# Revit family: EU_SINGLE_ODU_UB1_Ver.1.1
name_source: partatom
category: Mechanical Equipment
revit_build: Autodesk Revit 2016 (Build: 20150220_1215(x64)
units: mm (PartAtom-declared; Revit-internal decimal feet)

## family parameters
Always vertical = Yes
Cut with Voids When Loaded = No
Part Type = Normal
Room Calculation Point = No
Round Connector Dimension = Use Radius
Shared = No
Work Plane-Based = No

## types (26) — shared parameters
Fan Grill Height = 653.88 mm
Fan Grill Length = 580.00 mm
Free Content Downloads = -
Location = -
Manufacturer = SAMSUNG
Manufacturer Metadata = -
Notes = -
Product Documentation Link = -
Product Page URL = -
Sales Rep Locator = -
Serial Number = -
Subscribe for Update Alerts = -
System Served = -
URL = www.samsung.com

## per-type parameters (varying)
| type | Model | Net Weight | Refrigerant Type |
| 9.00 kW, 380-415V, HEAT PUMP | AC090MXADNH/EU | 72.00 kg | R410A |
| 10.00 kW, 380-415V, HEAT PUMP | AC100MXADNH/EU | 72.00 kg | R410A |
| 12.00 kW, 380-415V, HEAT PUMP | AC120MXADNH/EU | 77.00 kg | R410A |
| 10.00 kW, 220-240V, HEAT PUMP - A | AC100KXADEH/EU | 72.00 kg | R410A |
| 9.00 kW, 220-240V, HEAT PUMP | AC090MXADKH/EU | 72.00 kg | R410A |
| 10.00 kW, 220-240V, HEAT PUMP - B | AC100MXADKH/EU | 72.00 kg | R410A |
| 12.00 kW, 220-240V, HEAT PUMP(구모델) | AC120MXADKH/EU | 77.00 kg | R410A |
| 12.00 kW, 220-240V, HEAT PUMP(신모델) | AC120MXADKH/EU | 77.00 kg | R410A |
| Single Heat Pump, 10.0kW, 220-240, R32, AC100RN4DKG/EU | AC100RXADKG/EU | 72.00 kg | R32 |
| Single Heat Pump, 10.0kW, 380-415, R32, AC100RN4DKG/EU | AC100RXADNG/EU | 72.00 kg | R33 |
| Single Heat Pump, 12.0kW, 220-240, R32, AC120RN4DKG/EU | AC120RXADKG/EU | 77.00 kg | R34 |
| Single Heat Pump, 12.0kW, 380-415, R32, AC120RN4DKG/EU | AC120RXADNG/EU | 77.00 kg | R35 |
| Single Heat Pump, 10.0kW, 220-240, R32, AC100RN4PKG/EU | AC100RXADKG/EU | 72.00 kg | R38 |
| Single Heat Pump, 10.0kW, 380-415, R32, AC100RN4PKG/EU | AC100RXADNG/EU | 72.00 kg | R39 |
| Single Heat Pump, 12.0kW, 220-240, R32, AC120RN4PKG/EU | AC120RXADKG/EU | 77.00 kg | R40 |
| Single Heat Pump, 12.0kW, 380-415, R32, AC120RN4PKG/EU | AC120RXADNG/EU | 77.00 kg | R41 |
| Single Heat Pump, 10.0kW, 220-240, R32, AC100RNMDKG/EU | AC100RXADKG/EU | 72.00 kg | R44 |
| Single Heat Pump, 10.0kW, 380-415, R32, AC100RNMDKG/EU | AC100RXADNG/EU | 72.00 kg | R45 |
| Single Heat Pump, 12.0kW, 220-240, R32, AC120RNMDKG/EU | AC120RXADKG/EU | 77.00 kg | R46 |
| Single Heat Pump, 12.0kW, 380-415, R32, AC120RNMDKG/EU | AC120RXADNG/EU | 77.00 kg | R47 |
| Single Heat Pump, 10.0kW, 220-240, R32, AC100RNCDKG/EU | AC100RXADKG/EU | 72.00 kg | R50 |
| Single Heat Pump, 10.0kW, 380-415, R32, AC100RNCDKG/EU | AC100RXADNG/EU | 72.00 kg | R51 |
| Single Heat Pump, 12.0kW, 220-240, R32, AC120RNCDKG/EU | AC120RXADKG/EU | 77.00 kg | R52 |
| Single Heat Pump, 12.0kW, 380-415, R32, AC120RNCDKG/EU | AC120RXADNG/EU | 77.00 kg | R53 |
| Single Heat Pump, 10.0kW, 220-240, R32, AC100RNTDKG/EU | AC100RXADKG/EU | 72.00 kg | R56 |
| Single Heat Pump, 10.0kW, 380-415, R32, AC100RNTDKG/EU | AC100RXADNG/EU | 72.00 kg | R57 |

## geometry (parser evidence)
native form markers: Sweep x13
no freeform markers — native parametric forms only
